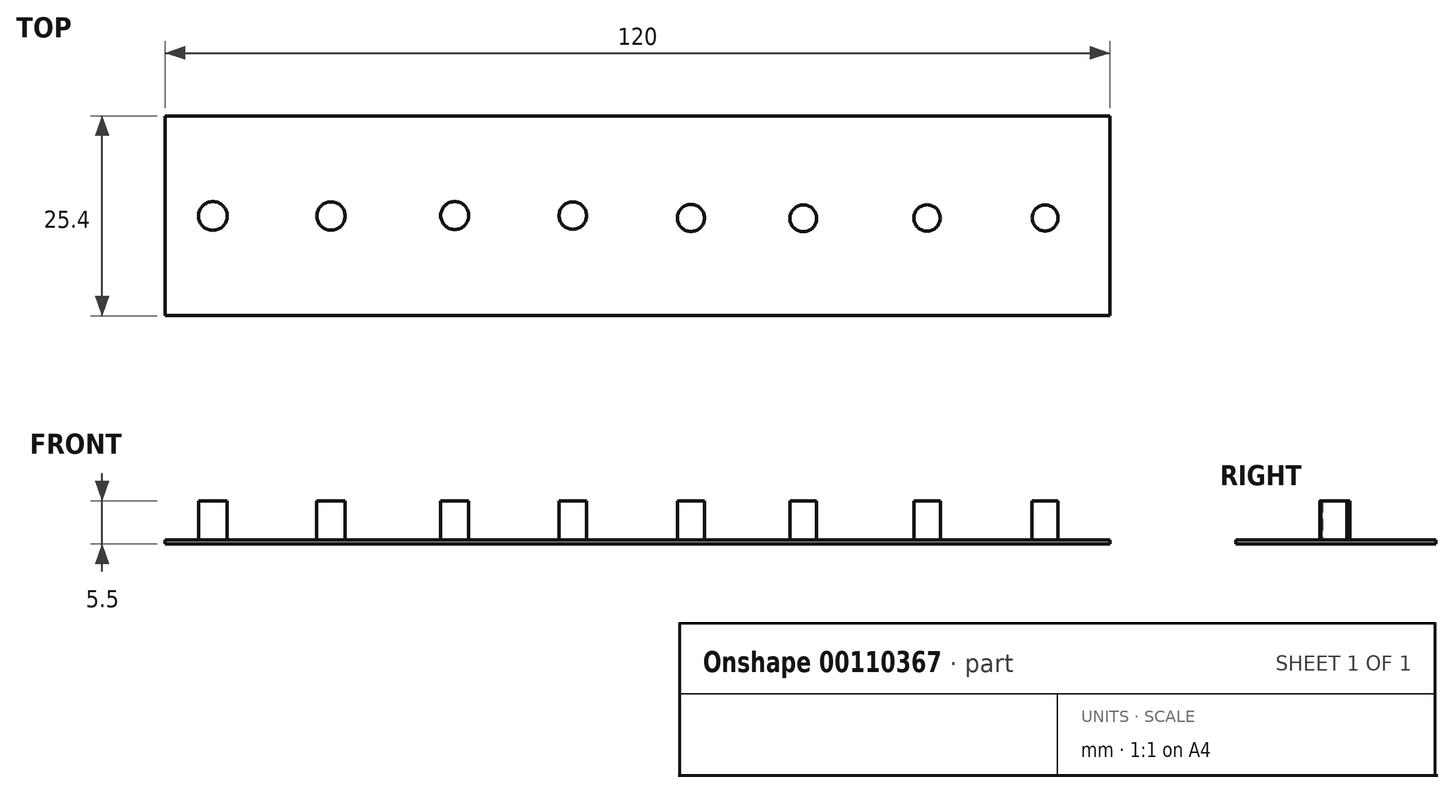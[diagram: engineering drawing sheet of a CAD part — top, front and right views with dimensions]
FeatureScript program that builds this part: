
annotation { "Feature Type Name" : "Feature", "Feature Type Description" : "" }
export const myFeature = defineFeature(function(context is Context, id is Id, definition is map)
    precondition{}
    {
        {
            var Q0;
            Q0=qCreatedBy(makeId("Top.planeOp"),FACE);
            var sketch = newSketch(context, id + "F0", { "sketchPlane" : qUnion([Q0])});
            skLineSegment(sketch, "E0.bottom", {"start": v(0, 0) * mm, "end": v(120, 0) * mm});
            skLineSegment(sketch, "E0.right", {"start": v(120, 0) * mm, "end": v(120, -25.4) * mm});
            skLineSegment(sketch, "E1.top", {"start": v(0, -25.4) * mm, "end": v(120, -25.4) * mm});
            skLineSegment(sketch, "E1.left", {"start": v(0, 0) * mm, "end": v(0, -25.4) * mm});
            skSolve(sketch);
        }
        {
            var Q0;
            Q0=makeQuery(id+"F0.imprint","IMPRINT",FACE,{"disambiguationData":[TD([[makeQuery(id+"F0.imprint","IMPRINT",EDGE,{"derivedFrom":sQuery(id+"F0.wireOp",EDGE,"E0.bottom")}),-1.0]])]});
            extrude(context, id + "F1", {"entities" : qUnion([Q0]), "offsetDistance" : 25 * mm, "depth" : 0.5 * mm});
        }
        {
            var Q0;
            Q0=makeQuery(id+"F1.opExtrude","CAP_FACE",FACE,{"disambiguationData":[OSD([sQuery(id+"F0.wireOp",EDGE,"E0.bottom"),sQuery(id+"F0.wireOp",EDGE,"E0.right"),sQuery(id+"F0.wireOp",EDGE,"E1.top"),sQuery(id+"F0.wireOp",EDGE,"E1.left")])],"isStart":false});
            var sketch = newSketch(context, id + "F2", { "sketchPlane" : qUnion([Q0])});
            skCircle(sketch, "E2", {"center": v(36.78, -12.67) * mm, "radius": 1.77 * mm});
            skCircle(sketch, "E3.1.0.0", {"center": v(51.78, -12.67) * mm, "radius": 1.75 * mm});
            skCircle(sketch, "E3.2.0.0", {"center": v(66.78, -12.97) * mm, "radius": 1.73 * mm});
            skCircle(sketch, "E3.4.0.0", {"center": v(96.78, -12.97) * mm, "radius": 1.68 * mm});
            skCircle(sketch, "E3.5.0.0", {"center": v(111.78, -12.97) * mm, "radius": 1.65 * mm});
            skCircle(sketch, "E4", {"center": v(6.06, -12.72) * mm, "radius": 1.82 * mm});
            skCircle(sketch, "E5.1.0.0", {"center": v(21.06, -12.72) * mm, "radius": 1.8 * mm});
            skCircle(sketch, "E5.5.0.0", {"center": v(81.06, -13.02) * mm, "radius": 1.7 * mm});
            skSolve(sketch);
        }
        {
            var Q0;
            Q0 = qSketchRegion(id + "F2", true);
            var Q1;
            Q1=sQuery(id+"F2.wireOp",EDGE,"E5.1.0.0");
            extrude(context, id + "F3", {"entities" : qUnion([Q0]), "surfaceEntities" : qUnion([Q1]), "offsetDistance" : 25 * mm, "depth" : 5 * mm});
        }
    });
